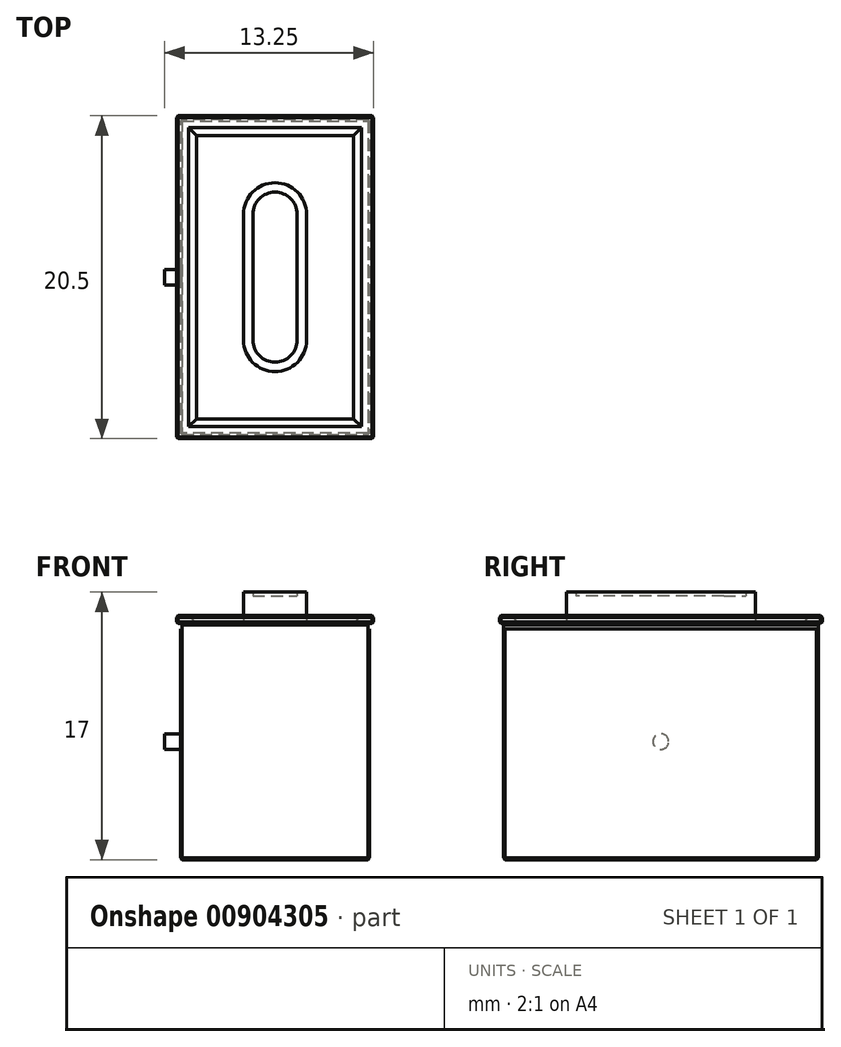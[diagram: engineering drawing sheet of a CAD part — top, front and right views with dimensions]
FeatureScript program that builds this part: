
annotation { "Feature Type Name" : "Feature", "Feature Type Description" : "" }
export const myFeature = defineFeature(function(context is Context, id is Id, definition is map)
    precondition{}
    {
        {
            var Q0;
            Q0=qCreatedBy(makeId("Front.planeOp"),FACE);
            var sketch = newSketch(context, id + "F0", { "sketchPlane" : qUnion([Q0])});
            skLineSegment(sketch, "E0.bottom", {"start": v(0, 0) * mm, "end": v(12, 0) * mm});
            skLineSegment(sketch, "E0.top", {"start": v(0, 15) * mm, "end": v(12, 15) * mm});
            skLineSegment(sketch, "E0.left", {"start": v(0, 0) * mm, "end": v(0, 15) * mm});
            skLineSegment(sketch, "E0.right", {"start": v(12, 0) * mm, "end": v(12, 15) * mm});
            skSolve(sketch);
        }
        {
            var Q0;
            Q0=makeQuery(id+"F0.imprint","IMPRINT",FACE,{"disambiguationData":[TD([[makeQuery(id+"F0.imprint","IMPRINT",EDGE,{"derivedFrom":sQuery(id+"F0.wireOp",EDGE,"E0.bottom")}),1.0]])]});
            extrude(context, id + "F1", {"entities" : qUnion([Q0]), "depth" : 20 * mm, "offsetDistance" : 25 * mm});
        }
        {
            var Q0;
            Q0=makeQuery(id+"F1.opExtrude","SWEPT_FACE",FACE,{"disambiguationData":[OSD([sQuery(id+"F0.wireOp",EDGE,"E0.left")])]});
            var sketch = newSketch(context, id + "F2", { "sketchPlane" : qUnion([Q0])});
            skLineSegment(sketch, "E1.0.0", {"start": v(0, 15) * mm, "end": v(0, 0) * mm});
            skLineSegment(sketch, "E1.0.1", {"start": v(0, 0) * mm, "end": v(20, 0) * mm});
            skLineSegment(sketch, "E1.0.2", {"start": v(20, 0) * mm, "end": v(20, 15) * mm});
            skLineSegment(sketch, "E1.0.3", {"start": v(20, 15) * mm, "end": v(0, 15) * mm});
            skLineSegment(sketch, "E2", {"start": v(0, 15) * mm, "end": v(20, 0) * mm});
            skCircle(sketch, "E3", {"center": v(10, 7.5) * mm, "radius": 0.5 * mm});
            skSolve(sketch);
        }
        {
            var Q0;
            {var subQ0=sQuery(id+"F2.wireOp",EDGE,"E3");var subQ1=sQuery(id+"F2.wireOp",EDGE,"E2");var subQ2=makeQuery(id+"F2.imprint","INTERSECT",VERTEX,{"disambiguationData":[OD(0.0)],"derivedFrom":[subQ1,subQ0]});Q0=makeQuery(id+"F2.imprint","IMPRINT",FACE,{"disambiguationData":[TD([[makeQuery(id+"F2.imprint","IMPRINT",EDGE,{"disambiguationData":[TD([[subQ2,-1.0]])],"derivedFrom":subQ1}),1.0]])]});}
            var Q1;
            {var subQ0=sQuery(id+"F2.wireOp",EDGE,"E3");var subQ1=sQuery(id+"F2.wireOp",EDGE,"E2");var subQ2=makeQuery(id+"F2.imprint","INTERSECT",VERTEX,{"disambiguationData":[OD(0.0)],"derivedFrom":[subQ1,subQ0]});Q1=makeQuery(id+"F2.imprint","IMPRINT",FACE,{"disambiguationData":[TD([[makeQuery(id+"F2.imprint","IMPRINT",EDGE,{"disambiguationData":[TD([[subQ2,-1.0]])],"derivedFrom":subQ1}),-1.0]])]});}
            extrude(context, id + "F3", {"entities" : qUnion([Q0, Q1]), "operationType" : NewBodyOperationType.ADD, "depth" : 1 * mm, "offsetDistance" : 25 * mm});
        }
        {
            var Q0;
            Q0=makeQuery(id+"F1.opExtrude","SWEPT_FACE",FACE,{"disambiguationData":[OSD([sQuery(id+"F0.wireOp",EDGE,"E0.top")])]});
            var sketch = newSketch(context, id + "F4", { "sketchPlane" : qUnion([Q0])});
            skLineSegment(sketch, "E4", {"start": v(0, 0) * mm, "end": v(12, -20) * mm});
            skLineSegment(sketch, "E5.bottom", {"start": v(12.25, 0.25) * mm, "end": v(-0.25, 0.25) * mm});
            skLineSegment(sketch, "E5.top", {"start": v(12.25, -20.25) * mm, "end": v(-0.25, -20.25) * mm});
            skLineSegment(sketch, "E5.left", {"start": v(12.25, 0.25) * mm, "end": v(12.25, -20.25) * mm});
            skLineSegment(sketch, "E5.right", {"start": v(-0.25, 0.25) * mm, "end": v(-0.25, -20.25) * mm});
            skPoint(sketch, "E5.middle", {"position": v(6, -10) * mm});
            skSolve(sketch);
        }
        {
            var Q0;
            Q0=makeQuery(id+"F4.imprint","IMPRINT",FACE,{"disambiguationData":[TD([[makeQuery(id+"F4.imprint","IMPRINT",EDGE,{"derivedFrom":sQuery(id+"F4.wireOp",EDGE,"E5.bottom")}),1.0]])]});
            var Q1;
            Q1=makeQuery(id+"F4.imprint","IMPRINT",FACE,{"disambiguationData":[TD([[makeQuery(id+"F4.imprint","IMPRINT",EDGE,{"derivedFrom":sQuery(id+"F4.wireOp",EDGE,"E4")}),1.0]])]});
            var Q2;
            Q2=makeQuery(id+"F4.imprint","IMPRINT",FACE,{"disambiguationData":[TD([[makeQuery(id+"F4.imprint","IMPRINT",EDGE,{"derivedFrom":sQuery(id+"F4.wireOp",EDGE,"E4")}),-1.0]])]});
            extrude(context, id + "F5", {"entities" : qUnion([Q0, Q1, Q2]), "operationType" : NewBodyOperationType.ADD, "depth" : 0.5 * mm, "offsetDistance" : 25 * mm});
        }
        {
            var Q0;
            Q0=makeQuery(id+"F5.opExtrude","CAP_FACE",FACE,{"disambiguationData":[OSD([sQuery(id+"F4.wireOp",EDGE,"E5.bottom"),sQuery(id+"F4.wireOp",EDGE,"E5.top"),sQuery(id+"F4.wireOp",EDGE,"E5.left"),sQuery(id+"F4.wireOp",EDGE,"E5.right")])],"isStart":false});
            var sketch = newSketch(context, id + "F6", { "sketchPlane" : qUnion([Q0])});
            skLineSegment(sketch, "E6", {"start": v(-0.25, 0.25) * mm, "end": v(12.25, -20.25) * mm});
            skLineSegment(sketch, "E7.bottom", {"start": v(11.5, -0.5) * mm, "end": v(0.5, -0.5) * mm});
            skLineSegment(sketch, "E7.top", {"start": v(11.5, -19.5) * mm, "end": v(0.5, -19.5) * mm});
            skLineSegment(sketch, "E7.left", {"start": v(11.5, -0.5) * mm, "end": v(11.5, -19.5) * mm});
            skLineSegment(sketch, "E7.right", {"start": v(0.5, -0.5) * mm, "end": v(0.5, -19.5) * mm});
            skPoint(sketch, "E7.middle", {"position": v(6, -10) * mm});
            skSolve(sketch);
        }
        {
            var Q0;
            {var subQ5=sQuery(id+"F6.wireOp",EDGE,"E7.top");Q0=makeQuery(id+"F6.imprint","IMPRINT",FACE,{"disambiguationData":[TD([[makeQuery(id+"F6.imprint","IMPRINT",EDGE,{"derivedFrom":subQ5}),-1.0]])]});}
            var Q1;
            {var subQ5=sQuery(id+"F6.wireOp",EDGE,"E7.bottom");Q1=makeQuery(id+"F6.imprint","IMPRINT",FACE,{"disambiguationData":[TD([[makeQuery(id+"F6.imprint","IMPRINT",EDGE,{"derivedFrom":subQ5}),1.0]])]});}
            extrude(context, id + "F7", {"entities" : qUnion([Q0, Q1]), "operationType" : NewBodyOperationType.REMOVE, "oppositeDirection" : true, "depth" : 0.5 * mm, "offsetDistance" : 25 * mm});
        }
        {
            var Q0;
            Q0=makeQuery(id+"F7.boolean.opBoolean","COPY",FACE,{"derivedFrom":makeQuery(id+"F7.opExtrude","CAP_FACE",FACE,{"disambiguationData":[OSD([sQuery(id+"F6.wireOp",EDGE,"E7.bottom"),sQuery(id+"F6.wireOp",EDGE,"E7.top"),sQuery(id+"F6.wireOp",EDGE,"E7.left"),sQuery(id+"F6.wireOp",EDGE,"E7.right")])],"isStart":false})});
            var sketch = newSketch(context, id + "F8", { "sketchPlane" : qUnion([Q0])});
            skLineSegment(sketch, "E8", {"start": v(0.5, -0.5) * mm, "end": v(11.5, -19.5) * mm});
            skLineSegment(sketch, "E9.bottom", {"start": v(8, -4) * mm, "end": v(4, -4) * mm});
            skLineSegment(sketch, "E9.top", {"start": v(8, -16) * mm, "end": v(4, -16) * mm});
            skLineSegment(sketch, "E9.left", {"start": v(8, -4) * mm, "end": v(8, -16) * mm});
            skLineSegment(sketch, "E9.right", {"start": v(4, -4) * mm, "end": v(4, -16) * mm});
            skPoint(sketch, "E9.middle", {"position": v(6, -10) * mm});
            skLineSegment(sketch, "E10.bottom", {"start": v(7.4, -4.6) * mm, "end": v(4.6, -4.6) * mm});
            skLineSegment(sketch, "E10.top", {"start": v(7.4, -15.4) * mm, "end": v(4.6, -15.4) * mm});
            skLineSegment(sketch, "E10.left", {"start": v(7.4, -4.6) * mm, "end": v(7.4, -15.4) * mm});
            skLineSegment(sketch, "E10.right", {"start": v(4.6, -4.6) * mm, "end": v(4.6, -15.4) * mm});
            skLineSegment(sketch, "E11", {"start": v(4.6, -6) * mm, "end": v(7.4, -6) * mm});
            skLineSegment(sketch, "E12", {"start": v(4.6, -14) * mm, "end": v(7.4, -14) * mm});
            skLineSegment(sketch, "E13", {"start": v(4, -6) * mm, "end": v(8, -6) * mm});
            skLineSegment(sketch, "E14", {"start": v(4, -14) * mm, "end": v(8, -14) * mm});
            skPoint(sketch, "E15", {"position": v(6, -4.6) * mm});
            skPoint(sketch, "E16", {"position": v(6, -4) * mm});
            skPoint(sketch, "E17", {"position": v(6, -15.4) * mm});
            skPoint(sketch, "E18", {"position": v(6, -16) * mm});
            skArc(sketch, "E19", {"start": v(7.4, -6) * mm, "mid": v(6, -4.6) * mm, "end": v(4.6, -6) * mm});
            skArc(sketch, "E20", {"start": v(8, -6) * mm, "mid": v(6, -4) * mm, "end": v(4, -6) * mm});
            skArc(sketch, "E21", {"start": v(4.6, -14) * mm, "mid": v(6, -15.4) * mm, "end": v(7.4, -14) * mm});
            skArc(sketch, "E22", {"start": v(4, -14) * mm, "mid": v(6, -16) * mm, "end": v(8, -14) * mm});
            skSolve(sketch);
        }
        {
            var Q0;
            {var subQ0=sQuery(id+"F8.wireOp",EDGE,"E9.right");var subQ1=sQuery(id+"F8.wireOp",EDGE,"E8");var subQ2=makeQuery(id+"F8.imprint","INTERSECT",VERTEX,{"derivedFrom":[subQ1,subQ0]});Q0=makeQuery(id+"F8.imprint","IMPRINT",FACE,{"disambiguationData":[TD([[makeQuery(id+"F8.imprint","IMPRINT",EDGE,{"disambiguationData":[TD([[subQ2,-1.0]])],"derivedFrom":subQ1}),-1.0]])]});}
            var Q1;
            {var subQ0=sQuery(id+"F8.wireOp",EDGE,"E9.right");var subQ1=sQuery(id+"F8.wireOp",EDGE,"E8");var subQ2=makeQuery(id+"F8.imprint","INTERSECT",VERTEX,{"derivedFrom":[subQ1,subQ0]});Q1=makeQuery(id+"F8.imprint","IMPRINT",FACE,{"disambiguationData":[TD([[makeQuery(id+"F8.imprint","IMPRINT",EDGE,{"disambiguationData":[TD([[subQ2,-1.0]])],"derivedFrom":subQ1}),1.0]])]});}
            var Q2;
            {var subQ1=sQuery(id+"F8.wireOp",EDGE,"E10.bottom");var subQ6=sQuery(id+"F8.wireOp",EDGE,"E10.left");var subQ7=makeQuery(id+"F8.imprint","INTERSECT",VERTEX,{"derivedFrom":[subQ1,subQ6]});Q2=makeQuery(id+"F8.imprint","IMPRINT",FACE,{"disambiguationData":[TD([[makeQuery(id+"F8.imprint","IMPRINT",EDGE,{"disambiguationData":[TD([[subQ7,-1.0]])],"derivedFrom":subQ1}),-1.0]])]});}
            var Q3;
            {var subQ0=sQuery(id+"F8.wireOp",EDGE,"E10.right");var subQ1=sQuery(id+"F8.wireOp",EDGE,"E10.bottom");var subQ2=makeQuery(id+"F8.imprint","INTERSECT",VERTEX,{"derivedFrom":[subQ1,subQ0]});Q3=makeQuery(id+"F8.imprint","IMPRINT",FACE,{"disambiguationData":[TD([[makeQuery(id+"F8.imprint","IMPRINT",EDGE,{"disambiguationData":[TD([[subQ2,1.0]])],"derivedFrom":subQ1}),1.0]])]});}
            var Q4;
            {var subQ0=sQuery(id+"F8.wireOp",EDGE,"E10.left");var subQ1=sQuery(id+"F8.wireOp",EDGE,"E10.bottom");var subQ2=makeQuery(id+"F8.imprint","INTERSECT",VERTEX,{"derivedFrom":[subQ1,subQ0]});Q4=makeQuery(id+"F8.imprint","IMPRINT",FACE,{"disambiguationData":[TD([[makeQuery(id+"F8.imprint","IMPRINT",EDGE,{"disambiguationData":[TD([[subQ2,-1.0]])],"derivedFrom":subQ1}),1.0]])]});}
            var Q5;
            {var subQ0=sQuery(id+"F8.wireOp",EDGE,"E10.left");var subQ1=sQuery(id+"F8.wireOp",EDGE,"E8");var subQ2=makeQuery(id+"F8.imprint","INTERSECT",VERTEX,{"derivedFrom":[subQ1,subQ0]});Q5=makeQuery(id+"F8.imprint","IMPRINT",FACE,{"disambiguationData":[TD([[makeQuery(id+"F8.imprint","IMPRINT",EDGE,{"disambiguationData":[TD([[subQ2,-1.0]])],"derivedFrom":subQ1}),1.0]])]});}
            var Q6;
            {var subQ0=sQuery(id+"F8.wireOp",EDGE,"E10.left");var subQ1=sQuery(id+"F8.wireOp",EDGE,"E8");var subQ2=makeQuery(id+"F8.imprint","INTERSECT",VERTEX,{"derivedFrom":[subQ1,subQ0]});Q6=makeQuery(id+"F8.imprint","IMPRINT",FACE,{"disambiguationData":[TD([[makeQuery(id+"F8.imprint","IMPRINT",EDGE,{"disambiguationData":[TD([[subQ2,-1.0]])],"derivedFrom":subQ1}),-1.0]])]});}
            var Q7;
            {var subQ1=sQuery(id+"F8.wireOp",EDGE,"E10.top");var subQ10=sQuery(id+"F8.wireOp",EDGE,"E10.left");var subQ11=makeQuery(id+"F8.imprint","INTERSECT",VERTEX,{"derivedFrom":[subQ1,subQ10]});Q7=makeQuery(id+"F8.imprint","IMPRINT",FACE,{"disambiguationData":[TD([[makeQuery(id+"F8.imprint","IMPRINT",EDGE,{"disambiguationData":[TD([[subQ11,-1.0]])],"derivedFrom":subQ1}),1.0]])]});}
            var Q8;
            {var subQ0=sQuery(id+"F8.wireOp",EDGE,"E10.left");var subQ1=sQuery(id+"F8.wireOp",EDGE,"E10.top");var subQ2=makeQuery(id+"F8.imprint","INTERSECT",VERTEX,{"derivedFrom":[subQ1,subQ0]});Q8=makeQuery(id+"F8.imprint","IMPRINT",FACE,{"disambiguationData":[TD([[makeQuery(id+"F8.imprint","IMPRINT",EDGE,{"disambiguationData":[TD([[subQ2,-1.0]])],"derivedFrom":subQ1}),-1.0]])]});}
            var Q9;
            {var subQ0=sQuery(id+"F8.wireOp",EDGE,"E10.right");var subQ1=sQuery(id+"F8.wireOp",EDGE,"E10.top");var subQ2=makeQuery(id+"F8.imprint","INTERSECT",VERTEX,{"derivedFrom":[subQ1,subQ0]});Q9=makeQuery(id+"F8.imprint","IMPRINT",FACE,{"disambiguationData":[TD([[makeQuery(id+"F8.imprint","IMPRINT",EDGE,{"disambiguationData":[TD([[subQ2,1.0]])],"derivedFrom":subQ1}),-1.0]])]});}
            extrude(context, id + "F9", {"entities" : qUnion([Q0, Q1, Q2, Q3, Q4, Q5, Q6, Q7, Q8, Q9]), "operationType" : NewBodyOperationType.ADD, "depth" : 2 * mm, "offsetDistance" : 25 * mm});
        }
        {
            var Q0;
            Q0=makeQuery(id+"F9.boolean.opBoolean","SPLIT",FACE,{"disambiguationData":[TD([makeQuery(id+"F9.opExtrude","SWEPT_FACE",FACE,{"disambiguationData":[OSD([sQuery(id+"F8.wireOp",EDGE,"E10.left")])]})])],"derivedFrom":makeQuery(id+"F7.boolean.opBoolean","COPY",FACE,{"derivedFrom":makeQuery(id+"F7.opExtrude","CAP_FACE",FACE,{"disambiguationData":[OSD([sQuery(id+"F6.wireOp",EDGE,"E7.bottom"),sQuery(id+"F6.wireOp",EDGE,"E7.top"),sQuery(id+"F6.wireOp",EDGE,"E7.left"),sQuery(id+"F6.wireOp",EDGE,"E7.right")])],"isStart":false})})});
            extrude(context, id + "F10", {"entities" : qUnion([Q0]), "operationType" : NewBodyOperationType.ADD, "depth" : 1.75 * mm, "offsetDistance" : 25 * mm});
        }
        {
            var Q0;
            Q0=makeQuery(id+"F1.opExtrude","CAP_EDGE",EDGE,{"disambiguationData":[OSD([sQuery(id+"F0.wireOp",EDGE,"E0.left")])],"isStart":true});
            var Q1;
            Q1=makeQuery(id+"F1.opExtrude","SWEPT_EDGE",EDGE,{"disambiguationData":[OSD([sQuery(id+"F0.wireOp",EDGE,"E0.bottom"),sQuery(id+"F0.wireOp",EDGE,"E0.left")])]});
            var Q2;
            Q2=makeQuery(id+"F1.opExtrude","CAP_EDGE",EDGE,{"disambiguationData":[OSD([sQuery(id+"F0.wireOp",EDGE,"E0.bottom")])],"isStart":true});
            var Q3;
            Q3=makeQuery(id+"F1.opExtrude","CAP_EDGE",EDGE,{"disambiguationData":[OSD([sQuery(id+"F0.wireOp",EDGE,"E0.left")])],"isStart":false});
            var Q4;
            Q4=makeQuery(id+"F1.opExtrude","CAP_EDGE",EDGE,{"disambiguationData":[OSD([sQuery(id+"F0.wireOp",EDGE,"E0.bottom")])],"isStart":false});
            var Q5;
            Q5=makeQuery(id+"F1.opExtrude","CAP_EDGE",EDGE,{"disambiguationData":[OSD([sQuery(id+"F0.wireOp",EDGE,"E0.right")])],"isStart":false});
            var Q6;
            Q6=makeQuery(id+"F1.opExtrude","CAP_EDGE",EDGE,{"disambiguationData":[OSD([sQuery(id+"F0.wireOp",EDGE,"E0.right")])],"isStart":true});
            var Q7;
            Q7=makeQuery(id+"F1.opExtrude","SWEPT_EDGE",EDGE,{"disambiguationData":[OSD([sQuery(id+"F0.wireOp",EDGE,"E0.bottom"),sQuery(id+"F0.wireOp",EDGE,"E0.right")])]});
            var Q8;
            Q8=makeQuery(id+"F5.opExtrude","SWEPT_EDGE",EDGE,{"disambiguationData":[OSD([sQuery(id+"F4.wireOp",EDGE,"E5.top"),sQuery(id+"F4.wireOp",EDGE,"E5.left")])]});
            var Q9;
            Q9=makeQuery(id+"F5.opExtrude","SWEPT_EDGE",EDGE,{"disambiguationData":[OSD([sQuery(id+"F4.wireOp",EDGE,"E5.bottom"),sQuery(id+"F4.wireOp",EDGE,"E5.left")])]});
            var Q10;
            Q10=makeQuery(id+"F5.opExtrude","CAP_EDGE",EDGE,{"disambiguationData":[OSD([sQuery(id+"F4.wireOp",EDGE,"E5.left")])],"isStart":true});
            var Q11;
            Q11=makeQuery(id+"F1.opExtrude","SWEPT_EDGE",EDGE,{"disambiguationData":[OSD([sQuery(id+"F0.wireOp",EDGE,"E0.top"),sQuery(id+"F0.wireOp",EDGE,"E0.right")])]});
            var Q12;
            Q12=makeQuery(id+"F1.opExtrude","CAP_EDGE",EDGE,{"disambiguationData":[OSD([sQuery(id+"F0.wireOp",EDGE,"E0.top")])],"isStart":false});
            var Q13;
            Q13=makeQuery(id+"F5.opExtrude","CAP_EDGE",EDGE,{"disambiguationData":[OSD([sQuery(id+"F4.wireOp",EDGE,"E5.top")])],"isStart":true});
            var Q14;
            Q14=makeQuery(id+"F1.opExtrude","SWEPT_EDGE",EDGE,{"disambiguationData":[OSD([sQuery(id+"F0.wireOp",EDGE,"E0.top"),sQuery(id+"F0.wireOp",EDGE,"E0.left")])]});
            var Q15;
            Q15=makeQuery(id+"F5.opExtrude","SWEPT_EDGE",EDGE,{"disambiguationData":[OSD([sQuery(id+"F4.wireOp",EDGE,"E5.top"),sQuery(id+"F4.wireOp",EDGE,"E5.right")])]});
            var Q16;
            Q16=makeQuery(id+"F5.opExtrude","CAP_EDGE",EDGE,{"disambiguationData":[OSD([sQuery(id+"F4.wireOp",EDGE,"E5.right")])],"isStart":true});
            var Q17;
            Q17=makeQuery(id+"F5.opExtrude","CAP_EDGE",EDGE,{"disambiguationData":[OSD([sQuery(id+"F4.wireOp",EDGE,"E5.bottom")])],"isStart":true});
            var Q18;
            Q18=makeQuery(id+"F5.opExtrude","SWEPT_EDGE",EDGE,{"disambiguationData":[OSD([sQuery(id+"F4.wireOp",EDGE,"E5.bottom"),sQuery(id+"F4.wireOp",EDGE,"E5.right")])]});
            var Q19;
            Q19=makeQuery(id+"F5.opExtrude","CAP_EDGE",EDGE,{"disambiguationData":[OSD([sQuery(id+"F4.wireOp",EDGE,"E5.bottom")])],"isStart":false});
            var Q20;
            Q20=makeQuery(id+"F5.opExtrude","CAP_EDGE",EDGE,{"disambiguationData":[OSD([sQuery(id+"F4.wireOp",EDGE,"E5.right")])],"isStart":false});
            var Q21;
            Q21=makeQuery(id+"F5.opExtrude","CAP_EDGE",EDGE,{"disambiguationData":[OSD([sQuery(id+"F4.wireOp",EDGE,"E5.left")])],"isStart":false});
            var Q22;
            Q22=makeQuery(id+"F5.opExtrude","CAP_EDGE",EDGE,{"disambiguationData":[OSD([sQuery(id+"F4.wireOp",EDGE,"E5.top")])],"isStart":false});
            chamfer(context, id + "F11", {"entities" : qUnion([Q0, Q1, Q2, Q3, Q4, Q5, Q6, Q7, Q8, Q9, Q10, Q11, Q12, Q13, Q14, Q15, Q16, Q17, Q18, Q19, Q20, Q21, Q22]), "width" : 0.1 * mm, "tangentPropagation" : true});
        }
        {
            var Q0;
            Q0=makeQuery(id+"F7.boolean.opBoolean","COPY",EDGE,{"derivedFrom":makeQuery(id+"F7.opExtrude","CAP_EDGE",EDGE,{"disambiguationData":[OSD([sQuery(id+"F6.wireOp",EDGE,"E7.right")])],"isStart":false})});
            var Q1;
            Q1=makeQuery(id+"F7.boolean.opBoolean","COPY",EDGE,{"derivedFrom":makeQuery(id+"F7.opExtrude","CAP_EDGE",EDGE,{"disambiguationData":[OSD([sQuery(id+"F6.wireOp",EDGE,"E7.bottom")])],"isStart":false})});
            var Q2;
            Q2=makeQuery(id+"F7.boolean.opBoolean","COPY",EDGE,{"derivedFrom":makeQuery(id+"F7.opExtrude","CAP_EDGE",EDGE,{"disambiguationData":[OSD([sQuery(id+"F6.wireOp",EDGE,"E7.left")])],"isStart":false})});
            var Q3;
            Q3=makeQuery(id+"F7.boolean.opBoolean","COPY",EDGE,{"derivedFrom":makeQuery(id+"F7.opExtrude","CAP_EDGE",EDGE,{"disambiguationData":[OSD([sQuery(id+"F6.wireOp",EDGE,"E7.top")])],"isStart":false})});
            var Q4;
            Q4=makeQuery(id+"F9.opExtrude","CAP_EDGE",EDGE,{"disambiguationData":[OSD([sQuery(id+"F8.wireOp",EDGE,"E9.left")])],"isStart":true});
            chamfer(context, id + "F12", {"entities" : qUnion([Q0, Q1, Q2, Q3, Q4]), "width" : 0.5 * mm, "tangentPropagation" : true});
        }
        {
            var Q0;
            Q0=makeQuery(id+"F1.opExtrude","CAP_FACE",FACE,{"disambiguationData":[OSD([sQuery(id+"F0.wireOp",EDGE,"E0.bottom"),sQuery(id+"F0.wireOp",EDGE,"E0.top"),sQuery(id+"F0.wireOp",EDGE,"E0.left"),sQuery(id+"F0.wireOp",EDGE,"E0.right")])],"isStart":false});
            var sketch = newSketch(context, id + "F13", { "sketchPlane" : qUnion([Q0])});
            skLineSegment(sketch, "E23.bottom", {"start": v(0.1, 14.9) * mm, "end": v(11.9, 14.9) * mm});
            skLineSegment(sketch, "E23.top", {"start": v(0.1, 14.4) * mm, "end": v(11.9, 14.4) * mm});
            skLineSegment(sketch, "E23.left", {"start": v(0.1, 14.9) * mm, "end": v(0.1, 14.4) * mm});
            skLineSegment(sketch, "E23.right", {"start": v(11.9, 14.9) * mm, "end": v(11.9, 14.4) * mm});
            skLineSegment(sketch, "E24.bottom", {"start": v(0.1, 14.4) * mm, "end": v(-2.32, 14.4) * mm});
            skLineSegment(sketch, "E24.top", {"start": v(0.1, 14.9) * mm, "end": v(-2.32, 14.9) * mm});
            skLineSegment(sketch, "E24.left", {"start": v(0.1, 14.4) * mm, "end": v(0.1, 14.9) * mm});
            skLineSegment(sketch, "E24.right", {"start": v(-2.32, 14.4) * mm, "end": v(-2.32, 14.9) * mm});
            skLineSegment(sketch, "E25.bottom", {"start": v(11.9, 14.4) * mm, "end": v(13.71, 14.4) * mm});
            skLineSegment(sketch, "E25.top", {"start": v(11.9, 14.9) * mm, "end": v(13.71, 14.9) * mm});
            skLineSegment(sketch, "E25.left", {"start": v(11.9, 14.4) * mm, "end": v(11.9, 14.9) * mm});
            skLineSegment(sketch, "E25.right", {"start": v(13.71, 14.4) * mm, "end": v(13.71, 14.9) * mm});
            skSolve(sketch);
        }
        {
            var Q0;
            Q0=makeQuery(id+"F13.imprint","IMPRINT",FACE,{"disambiguationData":[TD([[makeQuery(id+"F13.imprint","IMPRINT",EDGE,{"derivedFrom":sQuery(id+"F13.wireOp",EDGE,"E24.bottom")}),-1.0]])]});
            var Q1;
            Q1=makeQuery(id+"F13.imprint","IMPRINT",FACE,{"disambiguationData":[TD([[makeQuery(id+"F13.imprint","IMPRINT",EDGE,{"derivedFrom":sQuery(id+"F13.wireOp",EDGE,"E23.bottom")}),1.0]])]});
            var Q2;
            Q2=makeQuery(id+"F13.imprint","IMPRINT",FACE,{"disambiguationData":[TD([[makeQuery(id+"F13.imprint","IMPRINT",EDGE,{"derivedFrom":sQuery(id+"F13.wireOp",EDGE,"E25.bottom")}),1.0]])]});
            extrude(context, id + "F14", {"entities" : qUnion([Q0, Q1, Q2]), "operationType" : NewBodyOperationType.REMOVE, "oppositeDirection" : true, "depth" : 25 * mm, "offsetDistance" : 25 * mm});
        }
        {
            var Q0;
            Q0=makeQuery(id+"F14.boolean.opBoolean","COPY",FACE,{"derivedFrom":makeQuery(id+"F14.opExtrude","SWEPT_FACE",FACE,{"disambiguationData":[OSD([sQuery(id+"F13.wireOp",EDGE,"E23.top"),sQuery(id+"F13.wireOp",EDGE,"E24.bottom"),sQuery(id+"F13.wireOp",EDGE,"E25.bottom")])]})});
            extrude(context, id + "F15", {"entities" : qUnion([Q0]), "operationType" : NewBodyOperationType.ADD, "depth" : 0.25 * mm, "offsetDistance" : 25 * mm});
        }
    });
